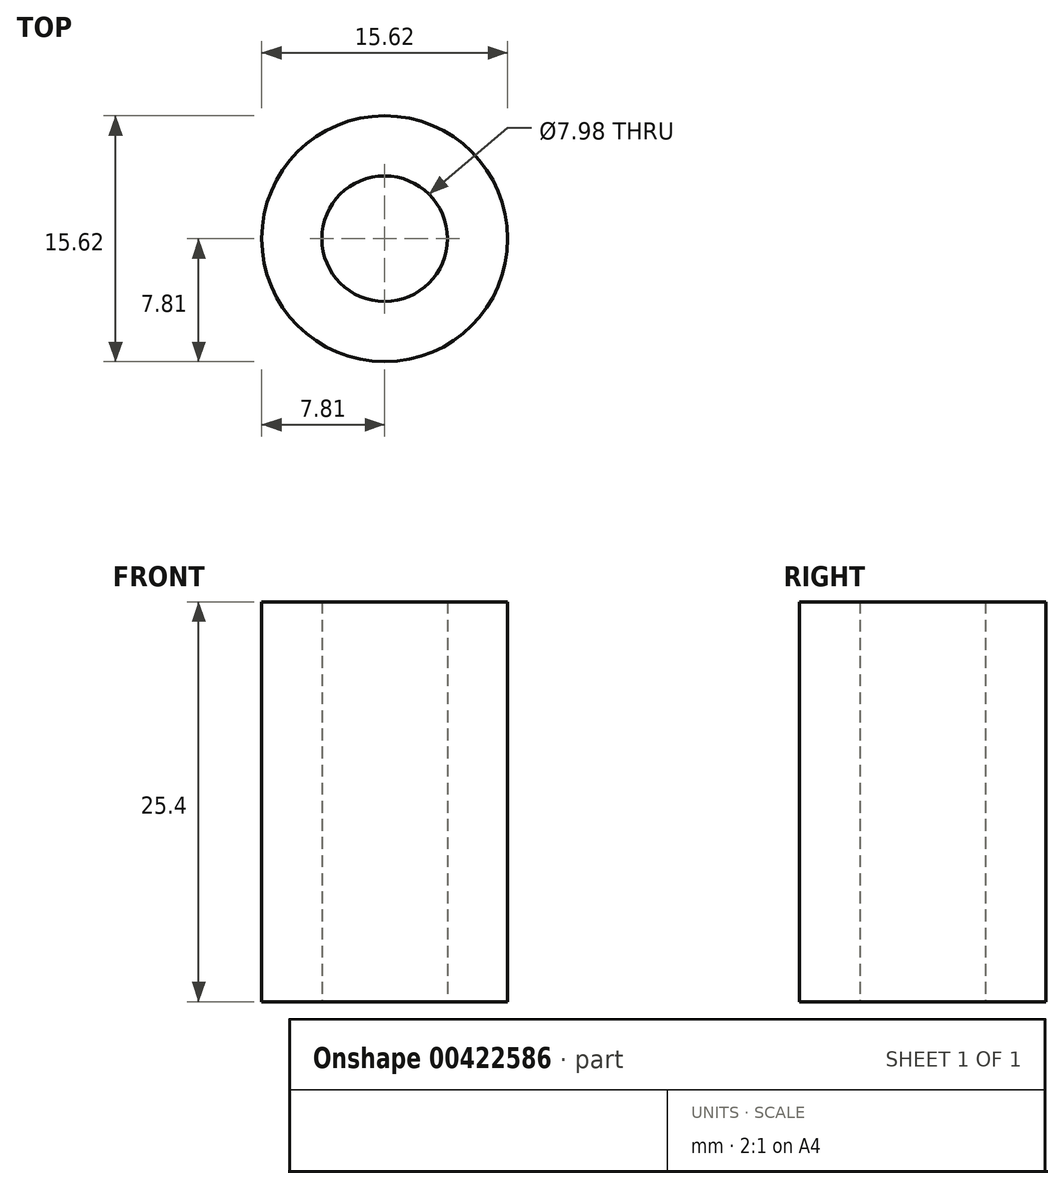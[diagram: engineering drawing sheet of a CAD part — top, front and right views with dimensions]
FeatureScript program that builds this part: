
annotation { "Feature Type Name" : "Feature", "Feature Type Description" : "" }
export const myFeature = defineFeature(function(context is Context, id is Id, definition is map)
    precondition{}
    {
        {
            var Q0;
            Q0=qCreatedBy(makeId("Top.planeOp"),FACE);
            var sketch = newSketch(context, id + "F0", { "sketchPlane" : qUnion([Q0])});
            skCircle(sketch, "E0", {"center": v(0, 0) * mm, "radius": 3.99 * mm});
            skCircle(sketch, "E1", {"center": v(0, 0) * mm, "radius": 7.81 * mm});
            skSolve(sketch);
        }
        {
            var Q0;
            Q0=makeQuery(id+"F0.imprint","IMPRINT",FACE,{"disambiguationData":[TD([[makeQuery(id+"F0.imprint","IMPRINT",EDGE,{"derivedFrom":sQuery(id+"F0.wireOp",EDGE,"E0")}),-1.0]])]});
            extrude(context, id + "F1", {"entities" : qUnion([Q0]), "depth" : 25.4 * mm});
        }
    });
